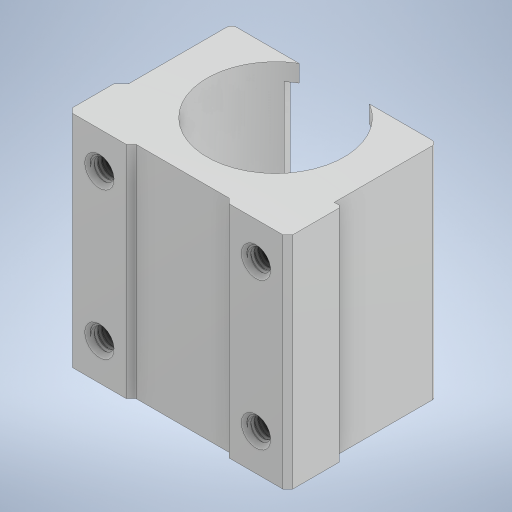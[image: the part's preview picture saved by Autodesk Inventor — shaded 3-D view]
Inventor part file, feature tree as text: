
AUTODESK INVENTOR PART (.ipt)
format: ipt  version: 2024 (Build 280153000, 153)  size: 2,371,072 bytes
history: native  units: in
note: dims shown in document units (in); Inventor stores cm internally (conversion verified against a paired STEP export)
features: extrude x1, sketch x1, other x1
ambient origin geometry x8: Origin, YZ Plane, XZ Plane, XY Plane, X Axis, Y Axis, Z Axis, Center Point
bodies: Solid4 (feature_tree)
feature tree (3):
  extrude  "Extrusion1"  [1 undecoded]
  sketch  "Sketch1"  dims[d0=3.937in d1=0.0in]
  other  "Guide support"
note: 1 required parameter value undecoded (feature->parameter linkage not recoverable at this tier; creation-order binding heuristic only, values carry confidence <= 0.55)
